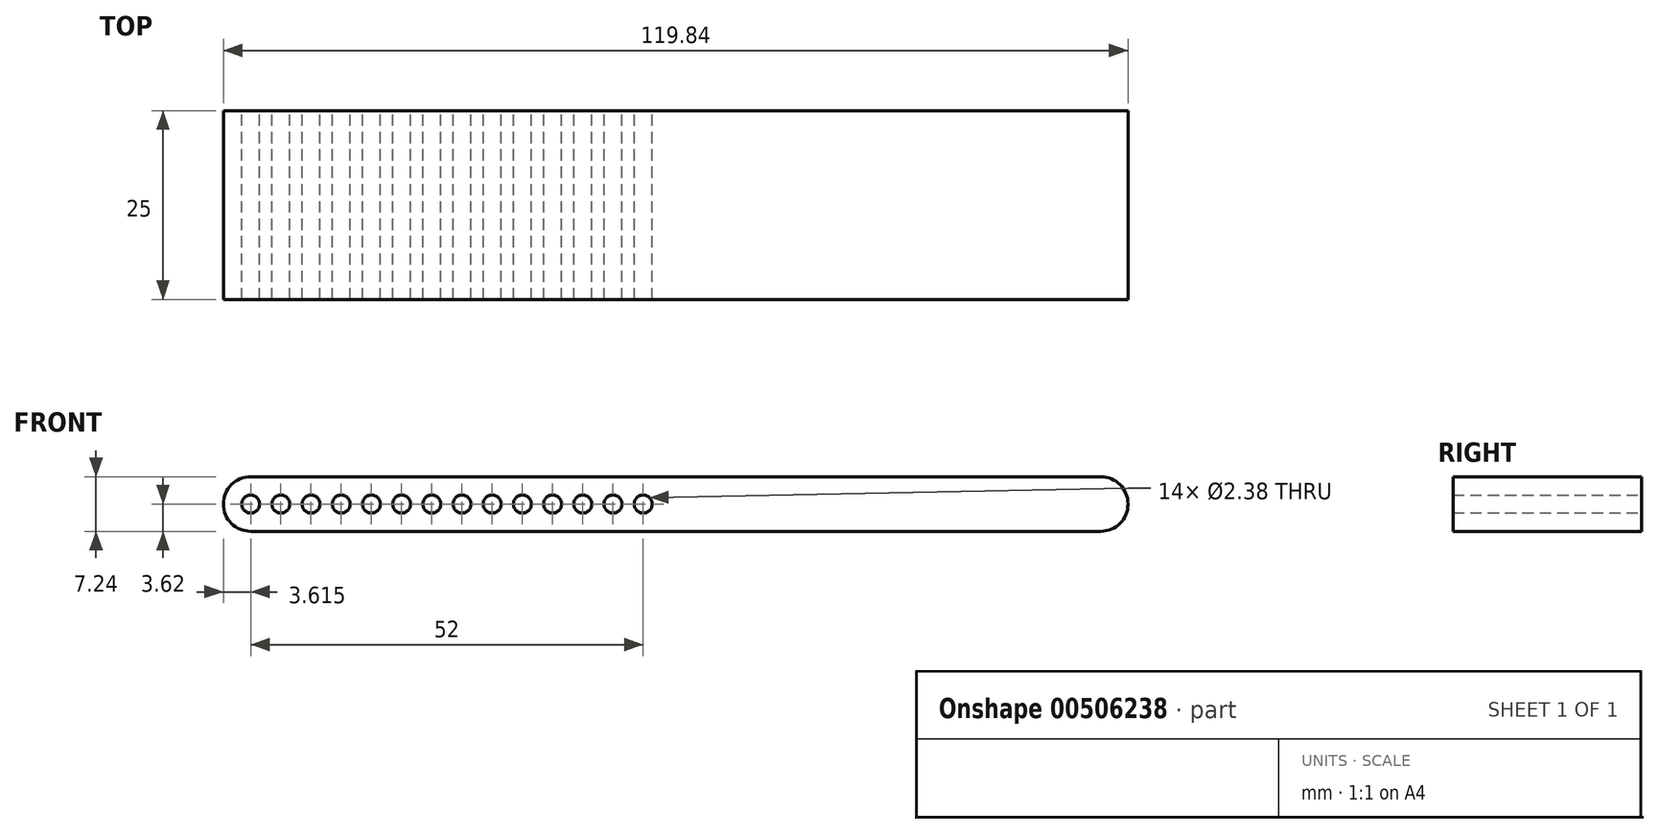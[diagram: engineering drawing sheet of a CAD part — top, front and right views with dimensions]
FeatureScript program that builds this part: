
annotation { "Feature Type Name" : "Feature", "Feature Type Description" : "" }
export const myFeature = defineFeature(function(context is Context, id is Id, definition is map)
    precondition{}
    {
        {
            var Q0;
            Q0=qCreatedBy(makeId("Front.planeOp"),FACE);
            var sketch = newSketch(context, id + "F0", { "sketchPlane" : qUnion([Q0])});
            skLineSegment(sketch, "E0.bottom", {"start": v(56.3, 3.62) * mm, "end": v(-56.3, 3.62) * mm});
            skLineSegment(sketch, "E0.top", {"start": v(56.3, -3.62) * mm, "end": v(-56.3, -3.62) * mm});
            skLineSegment(sketch, "E0.left", {"start": v(56.3, 3.62) * mm, "end": v(56.3, -3.62) * mm});
            skLineSegment(sketch, "E0.right", {"start": v(-56.3, 3.62) * mm, "end": v(-56.3, -3.62) * mm});
            skPoint(sketch, "E0.middle", {"position": v(0, 0) * mm});
            skArc(sketch, "E1", {"start": v(-56.3, 3.62) * mm, "mid": v(-59.92, 0) * mm, "end": v(-56.3, -3.61) * mm});
            skArc(sketch, "E2", {"start": v(56.3, -3.61) * mm, "mid": v(59.92, 0) * mm, "end": v(56.3, 3.62) * mm});
            skCircle(sketch, "E3", {"center": v(-56.3, 0) * mm, "radius": 1.2 * mm});
            skCircle(sketch, "E4.1.0.0", {"center": v(-52.3, 0) * mm, "radius": 1.2 * mm});
            skCircle(sketch, "E4.2.0.0", {"center": v(-48.3, 0) * mm, "radius": 1.2 * mm});
            skCircle(sketch, "E4.3.0.0", {"center": v(-44.3, 0) * mm, "radius": 1.2 * mm});
            skCircle(sketch, "E4.4.0.0", {"center": v(-40.3, 0) * mm, "radius": 1.2 * mm});
            skCircle(sketch, "E4.5.0.0", {"center": v(-36.3, 0) * mm, "radius": 1.2 * mm});
            skCircle(sketch, "E4.6.0.0", {"center": v(-32.3, 0) * mm, "radius": 1.2 * mm});
            skCircle(sketch, "E4.7.0.0", {"center": v(-28.3, 0) * mm, "radius": 1.2 * mm});
            skCircle(sketch, "E4.8.0.0", {"center": v(-24.3, 0) * mm, "radius": 1.2 * mm});
            skCircle(sketch, "E4.9.0.0", {"center": v(-20.3, 0) * mm, "radius": 1.2 * mm});
            skCircle(sketch, "E4.10.0.0", {"center": v(-16.3, 0) * mm, "radius": 1.2 * mm});
            skCircle(sketch, "E4.11.0.0", {"center": v(-12.3, 0) * mm, "radius": 1.2 * mm});
            skCircle(sketch, "E4.12.0.0", {"center": v(-8.3, 0) * mm, "radius": 1.2 * mm});
            skCircle(sketch, "E4.13.0.0", {"center": v(-4.3, 0) * mm, "radius": 1.2 * mm});
            skLineSegment(sketch, "E4.direction1", {"start": v(-56.3, 0) * mm, "end": v(-52.3, 0) * mm, "construction": true});
            skSolve(sketch);
        }
        {
            var Q0;
            Q0=makeQuery(id+"F0.imprint","IMPRINT",FACE,{"disambiguationData":[TD([[makeQuery(id+"F0.imprint","IMPRINT",EDGE,{"derivedFrom":sQuery(id+"F0.wireOp",EDGE,"E0.left")}),1.0]])]});
            var Q1;
            {var subQ0=sQuery(id+"F0.wireOp",EDGE,"E1");Q1=makeQuery(id+"F0.imprint","IMPRINT",FACE,{"disambiguationData":[TD([[makeQuery(id+"F0.imprint","IMPRINT",EDGE,{"derivedFrom":subQ0}),1.0]])]});}
            var Q2;
            {var subQ6=sQuery(id+"F0.wireOp",EDGE,"E0.bottom");Q2=makeQuery(id+"F0.imprint","IMPRINT",FACE,{"disambiguationData":[TD([[makeQuery(id+"F0.imprint","IMPRINT",EDGE,{"derivedFrom":subQ6}),1.0]])]});}
            extrude(context, id + "F1", {"entities" : qUnion([Q0, Q1, Q2]), "depth" : 25 * mm});
        }
    });
